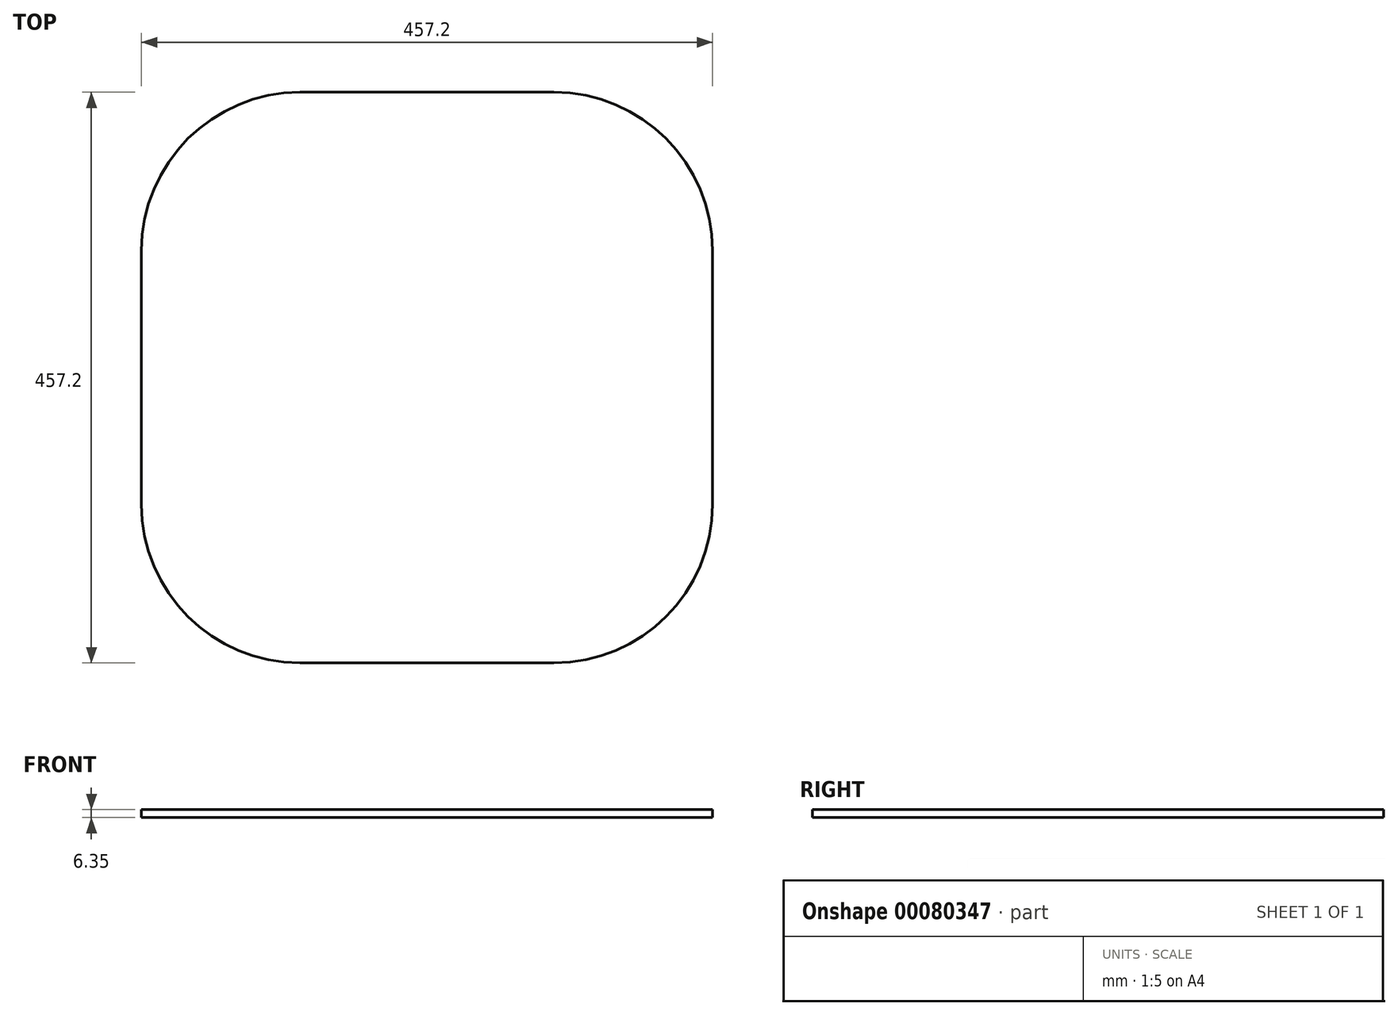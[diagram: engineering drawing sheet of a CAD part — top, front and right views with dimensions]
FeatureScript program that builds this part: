
annotation { "Feature Type Name" : "Feature", "Feature Type Description" : "" }
export const myFeature = defineFeature(function(context is Context, id is Id, definition is map)
    precondition{}
    {
        {
            var Q0;
            Q0=qCreatedBy(makeId("Top.planeOp"),FACE);
            var sketch = newSketch(context, id + "F0", { "sketchPlane" : qUnion([Q0])});
            skLineSegment(sketch, "E0.bottom", {"start": v(228.6, 228.6) * mm, "end": v(-228.6, 228.6) * mm});
            skLineSegment(sketch, "E0.top", {"start": v(228.6, -228.6) * mm, "end": v(-228.6, -228.6) * mm});
            skLineSegment(sketch, "E0.left", {"start": v(228.6, 228.6) * mm, "end": v(228.6, -228.6) * mm});
            skLineSegment(sketch, "E0.right", {"start": v(-228.6, 228.6) * mm, "end": v(-228.6, -228.6) * mm});
            skPoint(sketch, "E0.middle", {"position": v(0, 0) * mm});
            skSolve(sketch);
        }
        {
            var Q0;
            Q0=makeQuery(id+"F0.imprint","IMPRINT",FACE,{"disambiguationData":[TD([[makeQuery(id+"F0.imprint","IMPRINT",EDGE,{"derivedFrom":sQuery(id+"F0.wireOp",EDGE,"E0.bottom")}),1.0]])]});
            extrude(context, id + "F1", {"entities" : qUnion([Q0]), "depth" : 6.35 * mm});
        }
        {
            var Q0;
            Q0=makeQuery(id+"F1.opExtrude","SWEPT_EDGE",EDGE,{"disambiguationData":[OSD([sQuery(id+"F0.wireOp",EDGE,"E0.bottom"),sQuery(id+"F0.wireOp",EDGE,"E0.right")])]});
            var Q1;
            Q1=makeQuery(id+"F1.opExtrude","SWEPT_EDGE",EDGE,{"disambiguationData":[OSD([sQuery(id+"F0.wireOp",EDGE,"E0.bottom"),sQuery(id+"F0.wireOp",EDGE,"E0.left")])]});
            var Q2;
            Q2=makeQuery(id+"F1.opExtrude","SWEPT_EDGE",EDGE,{"disambiguationData":[OSD([sQuery(id+"F0.wireOp",EDGE,"E0.top"),sQuery(id+"F0.wireOp",EDGE,"E0.left")])]});
            var Q3;
            Q3=makeQuery(id+"F1.opExtrude","SWEPT_EDGE",EDGE,{"disambiguationData":[OSD([sQuery(id+"F0.wireOp",EDGE,"E0.top"),sQuery(id+"F0.wireOp",EDGE,"E0.right")])]});
            fillet(context, id + "F2", {"entities" : qUnion([Q0, Q1, Q2, Q3]), "radius" : 127 * mm, "tangentPropagation" : true, "allowEdgeOverflow" : false});
        }
    });
